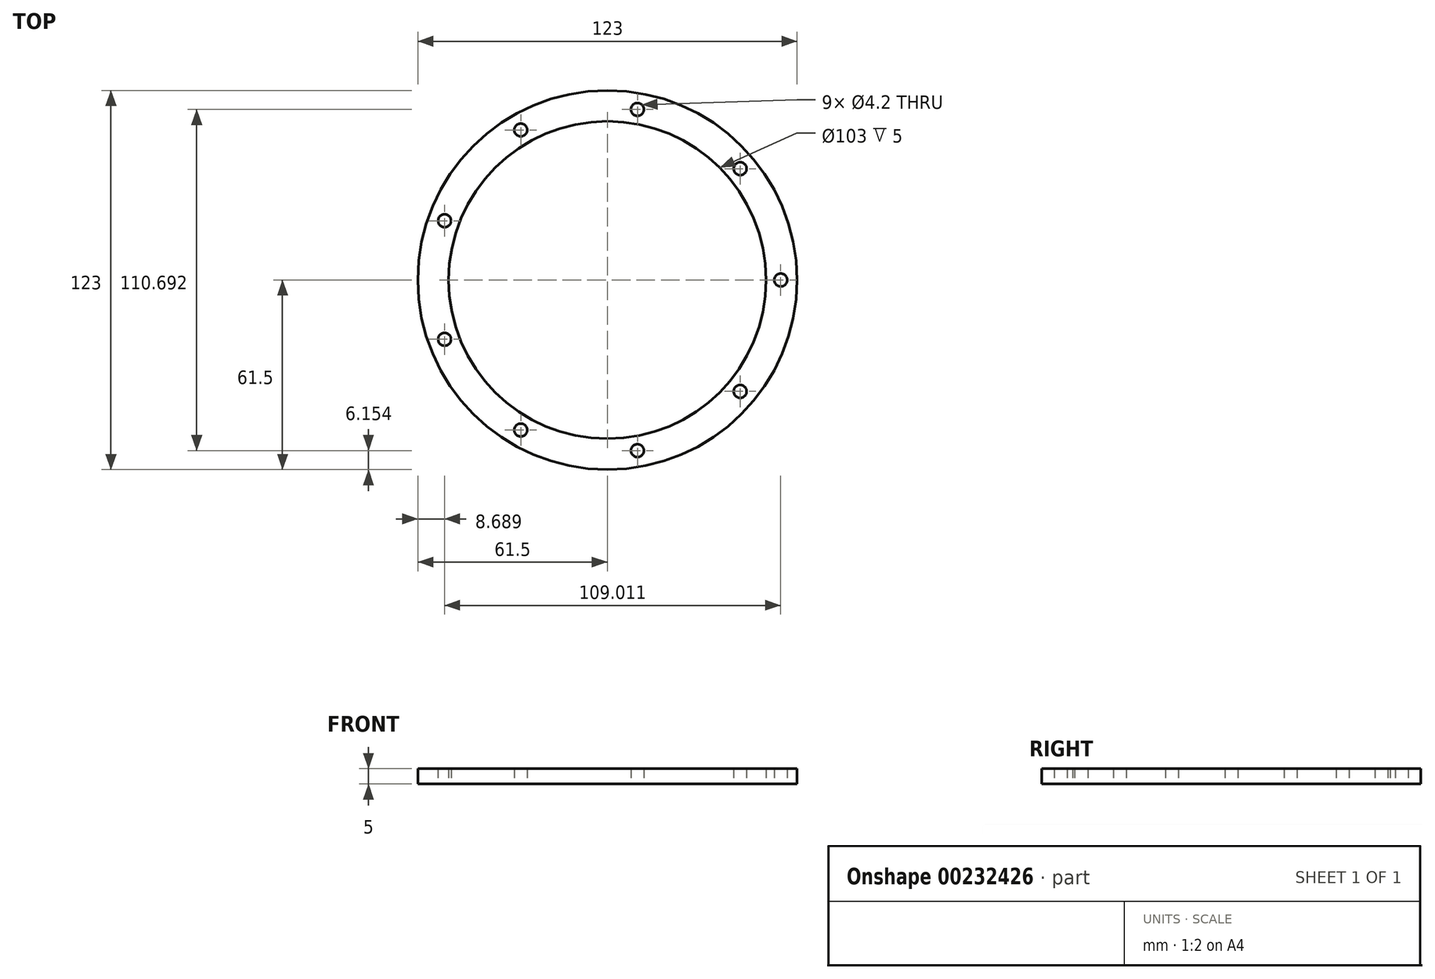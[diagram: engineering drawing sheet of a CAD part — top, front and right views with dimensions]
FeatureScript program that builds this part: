
annotation { "Feature Type Name" : "Feature", "Feature Type Description" : "" }
export const myFeature = defineFeature(function(context is Context, id is Id, definition is map)
    precondition{}
    {
        {
            var Q0;
            Q0=qCreatedBy(makeId("Top.planeOp"),FACE);
            var sketch = newSketch(context, id + "F0", { "sketchPlane" : qUnion([Q0])});
            skCircle(sketch, "E0", {"center": v(0, 0) * mm, "radius": 61.5 * mm});
            skCircle(sketch, "E1", {"center": v(0, 0) * mm, "radius": 51.5 * mm});
            skCircle(sketch, "E2", {"center": v(56.2, 0) * mm, "radius": 2.1 * mm});
            skCircle(sketch, "E3.1.0", {"center": v(43.05, 36.12) * mm, "radius": 2.1 * mm});
            skCircle(sketch, "E3.2.0", {"center": v(9.76, 55.35) * mm, "radius": 2.1 * mm});
            skCircle(sketch, "E3.3.0", {"center": v(-28.1, 48.67) * mm, "radius": 2.1 * mm});
            skCircle(sketch, "E3.4.0", {"center": v(-52.81, 19.22) * mm, "radius": 2.1 * mm});
            skCircle(sketch, "E3.5.0", {"center": v(-52.81, -19.22) * mm, "radius": 2.1 * mm});
            skCircle(sketch, "E3.6.0", {"center": v(-28.1, -48.67) * mm, "radius": 2.1 * mm});
            skCircle(sketch, "E3.7.0", {"center": v(9.76, -55.35) * mm, "radius": 2.1 * mm});
            skCircle(sketch, "E3.8.0", {"center": v(43.05, -36.12) * mm, "radius": 2.1 * mm});
            skSolve(sketch);
        }
        {
            var Q0;
            Q0=makeQuery(id+"F0.imprint","IMPRINT",FACE,{"disambiguationData":[TD([[makeQuery(id+"F0.imprint","IMPRINT",EDGE,{"derivedFrom":sQuery(id+"F0.wireOp",EDGE,"E0")}),1.0]])]});
            extrude(context, id + "F1", {"entities" : qUnion([Q0]), "endBound" : BoundingType.SYMMETRIC, "depth" : 5 * mm});
        }
    });
